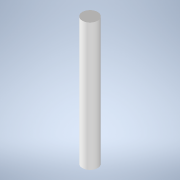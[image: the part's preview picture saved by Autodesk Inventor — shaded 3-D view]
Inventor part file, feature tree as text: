
AUTODESK INVENTOR PART (.ipt)
format: ipt  version: 2022 (Build 260153000, 153)  size: 91,136 bytes
history: native  units: mm
features: extrude x1, sketch x1
ambient origin geometry x8: Origin, YZ Plane, XZ Plane, XY Plane, X Axis, Y Axis, Z Axis, Center Point
bodies: Volumenkörper1 (feature_tree)
feature tree (2):
  extrude  "Extrusion1"  Depth=50.0mm TaperAngle=0.0deg
  sketch  "Skizze1"  dims[d0=6.0mm d1=50.0mm d2=0.0mm]
